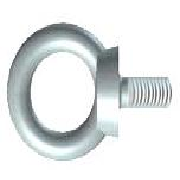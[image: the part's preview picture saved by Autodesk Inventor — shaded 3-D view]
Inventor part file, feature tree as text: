
AUTODESK INVENTOR PART (.ipt)
format: ipt  version: 2024 (Build 280153000, 153)  size: 276,992 bytes
history: native  units: mm (DEFAULTED — no unit token found)
features: extrude x2, other x1
ambient origin geometry x8: Origin, YZ Plane, XZ Plane, XY Plane, X Axis, Y Axis, Z Axis, Center Point
bodies: Solid1 (feature_tree), Body (feature_tree)
feature tree (3):
  extrude  "Eye"  Depth=35.0mm
  extrude  "Cut"  Depth=72.0mm
  other  "Groove1"
